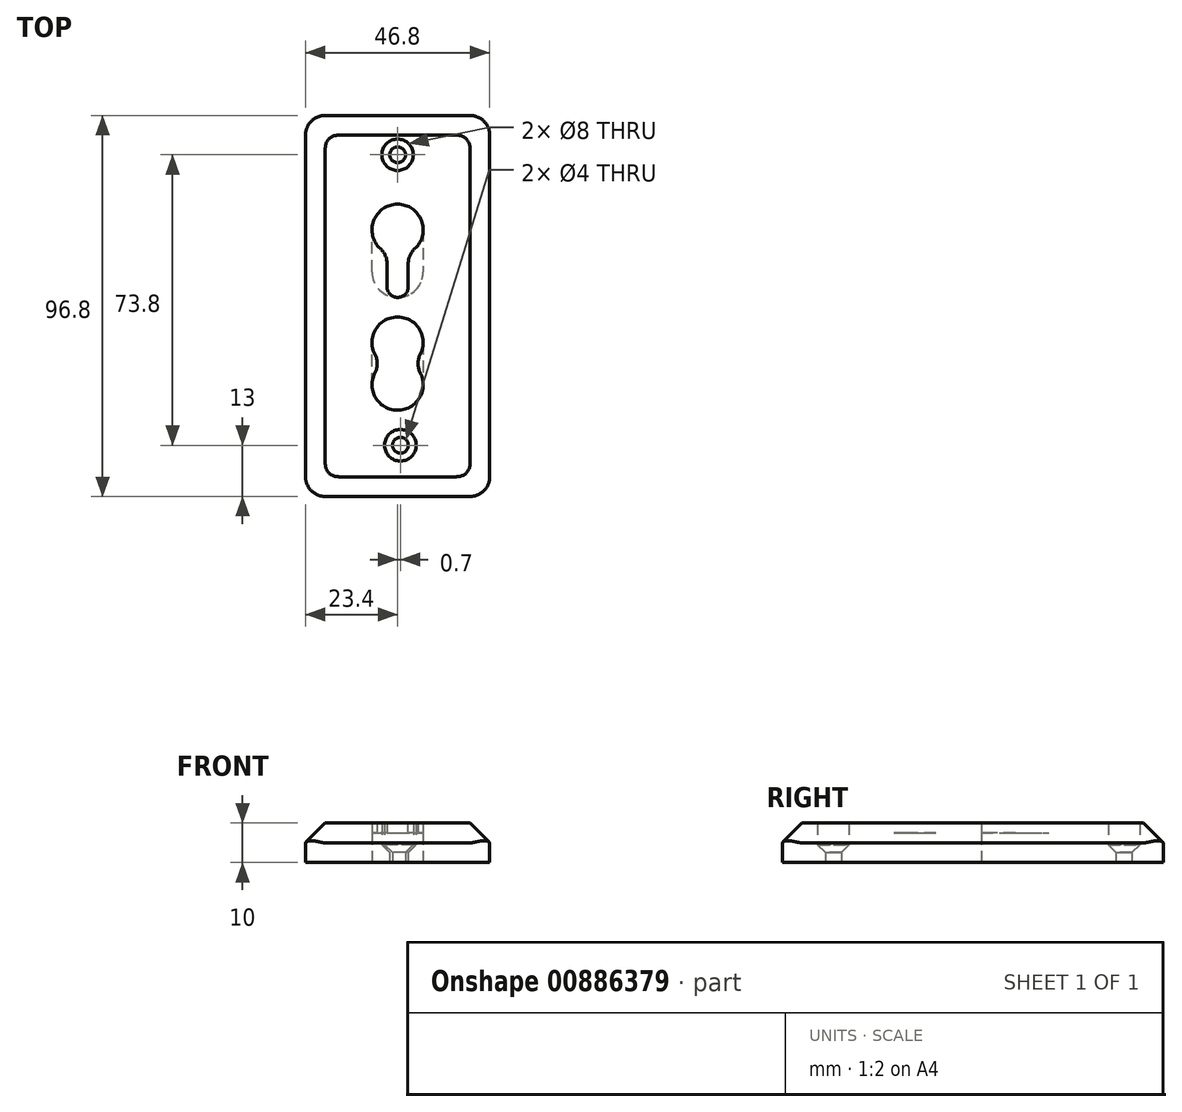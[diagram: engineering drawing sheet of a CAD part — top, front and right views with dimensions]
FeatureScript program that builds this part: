
annotation { "Feature Type Name" : "Feature", "Feature Type Description" : "" }
export const myFeature = defineFeature(function(context is Context, id is Id, definition is map)
    precondition{}
    {
        {
            var Q0;
            Q0=qCreatedBy(makeId("Top.planeOp"),FACE);
            var sketch = newSketch(context, id + "F0", { "sketchPlane" : qUnion([Q0])});
            skLineSegment(sketch, "E0", {"start": v(19.1, -41.4) * mm, "end": v(-17.7, -41.4) * mm});
            skCircle(sketch, "E1", {"center": v(0, -7.3) * mm, "radius": 6.5 * mm});
            skLineSegment(sketch, "E2", {"start": v(0, -7.3) * mm, "end": v(2.7, -7.3) * mm});
            skLineSegment(sketch, "E3.bottom", {"start": v(2.7, -7.3) * mm, "end": v(-2.7, -7.3) * mm});
            skLineSegment(sketch, "E4.top", {"start": v(-23.4, -46.4) * mm, "end": v(23.4, -46.4) * mm});
            skLineSegment(sketch, "E5", {"start": v(2.7, -7.3) * mm, "end": v(2.7, -21.8) * mm});
            skLineSegment(sketch, "E6", {"start": v(-2.7, -21.8) * mm, "end": v(-2.7, -7.3) * mm});
            skArc(sketch, "E7", {"start": v(2.7, -21.8) * mm, "mid": v(0, -24.5) * mm, "end": v(-2.7, -21.8) * mm});
            skLineSegment(sketch, "E8", {"start": v(0.7, -41.4) * mm, "end": v(0.7, -33.4) * mm});
            skCircle(sketch, "E9", {"center": v(0.7, -33.4) * mm, "radius": 2 * mm});
            skCircle(sketch, "E10", {"center": v(0.7, -33.4) * mm, "radius": 4 * mm});
            skLineSegment(sketch, "E11", {"start": v(19.1, 45.4) * mm, "end": v(-17.7, 45.4) * mm});
            skLineSegment(sketch, "E12", {"start": v(-17.7, 45.4) * mm, "end": v(-17.7, -41.4) * mm});
            skLineSegment(sketch, "E13", {"start": v(19.1, 45.4) * mm, "end": v(19.1, -41.4) * mm});
            skLineSegment(sketch, "E14", {"start": v(23.4, 50.4) * mm, "end": v(-23.4, 50.4) * mm});
            skLineSegment(sketch, "E15", {"start": v(-23.4, 50.4) * mm, "end": v(-23.4, -46.4) * mm});
            skLineSegment(sketch, "E16", {"start": v(23.4, 50.4) * mm, "end": v(23.4, -46.4) * mm});
            skLineSegment(sketch, "E17", {"start": v(0, 45.4) * mm, "end": v(0, 40.4) * mm});
            skCircle(sketch, "E18", {"center": v(0, 40.4) * mm, "radius": 2 * mm});
            skCircle(sketch, "E19", {"center": v(0, 40.4) * mm, "radius": 4 * mm});
            skCircle(sketch, "E20", {"center": v(0, -18) * mm, "radius": 6.5 * mm});
            skCircle(sketch, "E21", {"center": v(0, 21.35) * mm, "radius": 6.5 * mm});
            skLineSegment(sketch, "E22", {"start": v(0, 21.35) * mm, "end": v(2.7, 21.35) * mm});
            skLineSegment(sketch, "E23", {"start": v(2.7, 21.35) * mm, "end": v(2.7, 6.85) * mm});
            skLineSegment(sketch, "E24", {"start": v(-2.7, 6.85) * mm, "end": v(-2.7, 21.35) * mm});
            skLineSegment(sketch, "E25", {"start": v(-2.7, 21.35) * mm, "end": v(2.7, 21.35) * mm});
            skArc(sketch, "E26", {"start": v(2.7, 6.85) * mm, "mid": v(0, 4.15) * mm, "end": v(-2.7, 6.85) * mm});
            skCircle(sketch, "E27", {"center": v(0, 10.65) * mm, "radius": 6.5 * mm});
            skLineSegment(sketch, "E28", {"start": v(-6.5, 10.65) * mm, "end": v(-6.5, 21.35) * mm});
            skLineSegment(sketch, "E29", {"start": v(6.5, 21.35) * mm, "end": v(6.5, 10.65) * mm});
            skLineSegment(sketch, "E30", {"start": v(-6.5, -18) * mm, "end": v(-6.5, -7.3) * mm});
            skLineSegment(sketch, "E31", {"start": v(6.5, -7.3) * mm, "end": v(6.5, -18) * mm});
            skSolve(sketch);
        }
        {
            var Q0;
            Q0=makeQuery(id+"F0.imprint","IMPRINT",FACE,{"disambiguationData":[TD([[makeQuery(id+"F0.imprint","IMPRINT",EDGE,{"derivedFrom":sQuery(id+"F0.wireOp",EDGE,"E4.top")}),1.0]])]});
            var Q1;
            Q1=makeQuery(id+"F0.imprint","IMPRINT",FACE,{"disambiguationData":[TD([[makeQuery(id+"F0.imprint","IMPRINT",EDGE,{"derivedFrom":sQuery(id+"F0.wireOp",EDGE,"E10")}),-1.0]])]});
            var Q2;
            {var subQ0=sQuery(id+"F0.wireOp",EDGE,"E28");Q2=makeQuery(id+"F0.imprint","IMPRINT",FACE,{"disambiguationData":[TD([[makeQuery(id+"F0.imprint","IMPRINT",EDGE,{"derivedFrom":subQ0}),-1.0]])]});}
            var Q3;
            {var subQ0=sQuery(id+"F0.wireOp",EDGE,"E27");var subQ2=sQuery(id+"F0.wireOp",EDGE,"E21");var subQ3=makeQuery(id+"F0.imprint","INTERSECT",VERTEX,{"disambiguationData":[OD(0.0)],"derivedFrom":[subQ2,subQ0]});Q3=makeQuery(id+"F0.imprint","IMPRINT",FACE,{"disambiguationData":[TD([[makeQuery(id+"F0.imprint","IMPRINT",EDGE,{"disambiguationData":[TD([[subQ3,-1.0]])],"derivedFrom":subQ2}),-1.0]])]});}
            var Q4;
            {var subQ2=sQuery(id+"F0.wireOp",EDGE,"E21");var subQ5=sQuery(id+"F0.wireOp",EDGE,"E23");var subQ7=makeQuery(id+"F0.imprint","INTERSECT",VERTEX,{"derivedFrom":[subQ2,subQ5]});Q4=makeQuery(id+"F0.imprint","IMPRINT",FACE,{"disambiguationData":[TD([[makeQuery(id+"F0.imprint","IMPRINT",EDGE,{"disambiguationData":[TD([[subQ7,-1.0]])],"derivedFrom":subQ2}),-1.0]])]});}
            var Q5;
            {var subQ0=sQuery(id+"F0.wireOp",EDGE,"E29");Q5=makeQuery(id+"F0.imprint","IMPRINT",FACE,{"disambiguationData":[TD([[makeQuery(id+"F0.imprint","IMPRINT",EDGE,{"derivedFrom":subQ0}),-1.0]])]});}
            var Q6;
            {var subQ0=sQuery(id+"F0.wireOp",EDGE,"E30");Q6=makeQuery(id+"F0.imprint","IMPRINT",FACE,{"disambiguationData":[TD([[makeQuery(id+"F0.imprint","IMPRINT",EDGE,{"derivedFrom":subQ0}),-1.0]])]});}
            var Q7;
            {var subQ0=sQuery(id+"F0.wireOp",EDGE,"E20");var subQ9=makeQuery(id+"F0.imprint","IMPRINT",VERTEX,{"disambiguationData":[OD(1.0)],"derivedFrom":subQ0});Q7=makeQuery(id+"F0.imprint","IMPRINT",FACE,{"disambiguationData":[TD([[makeQuery(id+"F0.imprint","IMPRINT",EDGE,{"disambiguationData":[TD([[subQ9,1.0]])],"derivedFrom":subQ0}),1.0]])]});}
            var Q8;
            {var subQ0=sQuery(id+"F0.wireOp",EDGE,"E20");var subQ2=makeQuery(id+"F0.imprint","IMPRINT",VERTEX,{"disambiguationData":[OD(0.0)],"derivedFrom":subQ0});Q8=makeQuery(id+"F0.imprint","IMPRINT",FACE,{"disambiguationData":[TD([[makeQuery(id+"F0.imprint","IMPRINT",EDGE,{"disambiguationData":[TD([[subQ2,-1.0]])],"derivedFrom":subQ0}),1.0]])]});}
            var Q9;
            {var subQ0=sQuery(id+"F0.wireOp",EDGE,"E31");Q9=makeQuery(id+"F0.imprint","IMPRINT",FACE,{"disambiguationData":[TD([[makeQuery(id+"F0.imprint","IMPRINT",EDGE,{"derivedFrom":subQ0}),-1.0]])]});}
            extrude(context, id + "F1", {"entities" : qUnion([Q0, Q1, Q2, Q3, Q4, Q5, Q6, Q7, Q8, Q9]), "depth" : 10 * mm, "offsetDistance" : 25 * mm});
        }
        {
            var Q0;
            Q0=makeQuery(id+"F0.imprint","IMPRINT",FACE,{"disambiguationData":[TD([[makeQuery(id+"F0.imprint","IMPRINT",EDGE,{"derivedFrom":sQuery(id+"F0.wireOp",EDGE,"E9")}),-1.0]])]});
            var Q1;
            Q1=makeQuery(id+"F0.imprint","IMPRINT",FACE,{"disambiguationData":[TD([[makeQuery(id+"F0.imprint","IMPRINT",EDGE,{"derivedFrom":sQuery(id+"F0.wireOp",EDGE,"E18")}),-1.0]])]});
            extrude(context, id + "F2", {"entities" : qUnion([Q0, Q1]), "operationType" : NewBodyOperationType.ADD, "depth" : 5 * mm, "offsetDistance" : 25 * mm});
        }
        {
            var Q0;
            {var subQ0=sQuery(id+"F0.wireOp",EDGE,"E29");Q0=makeQuery(id+"F0.imprint","IMPRINT",FACE,{"disambiguationData":[TD([[makeQuery(id+"F0.imprint","IMPRINT",EDGE,{"derivedFrom":subQ0}),-1.0]])]});}
            var Q1;
            {var subQ2=sQuery(id+"F0.wireOp",EDGE,"E21");var subQ5=sQuery(id+"F0.wireOp",EDGE,"E23");var subQ7=makeQuery(id+"F0.imprint","INTERSECT",VERTEX,{"derivedFrom":[subQ2,subQ5]});Q1=makeQuery(id+"F0.imprint","IMPRINT",FACE,{"disambiguationData":[TD([[makeQuery(id+"F0.imprint","IMPRINT",EDGE,{"disambiguationData":[TD([[subQ7,-1.0]])],"derivedFrom":subQ2}),-1.0]])]});}
            var Q2;
            {var subQ0=sQuery(id+"F0.wireOp",EDGE,"E27");var subQ2=sQuery(id+"F0.wireOp",EDGE,"E21");var subQ3=makeQuery(id+"F0.imprint","INTERSECT",VERTEX,{"disambiguationData":[OD(0.0)],"derivedFrom":[subQ2,subQ0]});Q2=makeQuery(id+"F0.imprint","IMPRINT",FACE,{"disambiguationData":[TD([[makeQuery(id+"F0.imprint","IMPRINT",EDGE,{"disambiguationData":[TD([[subQ3,-1.0]])],"derivedFrom":subQ2}),-1.0]])]});}
            var Q3;
            {var subQ0=sQuery(id+"F0.wireOp",EDGE,"E28");Q3=makeQuery(id+"F0.imprint","IMPRINT",FACE,{"disambiguationData":[TD([[makeQuery(id+"F0.imprint","IMPRINT",EDGE,{"derivedFrom":subQ0}),-1.0]])]});}
            var Q4;
            {var subQ0=sQuery(id+"F0.wireOp",EDGE,"E30");Q4=makeQuery(id+"F0.imprint","IMPRINT",FACE,{"disambiguationData":[TD([[makeQuery(id+"F0.imprint","IMPRINT",EDGE,{"derivedFrom":subQ0}),-1.0]])]});}
            var Q5;
            {var subQ0=sQuery(id+"F0.wireOp",EDGE,"E20");var subQ9=makeQuery(id+"F0.imprint","IMPRINT",VERTEX,{"disambiguationData":[OD(1.0)],"derivedFrom":subQ0});Q5=makeQuery(id+"F0.imprint","IMPRINT",FACE,{"disambiguationData":[TD([[makeQuery(id+"F0.imprint","IMPRINT",EDGE,{"disambiguationData":[TD([[subQ9,1.0]])],"derivedFrom":subQ0}),1.0]])]});}
            var Q6;
            {var subQ0=sQuery(id+"F0.wireOp",EDGE,"E20");var subQ2=makeQuery(id+"F0.imprint","IMPRINT",VERTEX,{"disambiguationData":[OD(0.0)],"derivedFrom":subQ0});Q6=makeQuery(id+"F0.imprint","IMPRINT",FACE,{"disambiguationData":[TD([[makeQuery(id+"F0.imprint","IMPRINT",EDGE,{"disambiguationData":[TD([[subQ2,-1.0]])],"derivedFrom":subQ0}),1.0]])]});}
            var Q7;
            {var subQ0=sQuery(id+"F0.wireOp",EDGE,"E31");Q7=makeQuery(id+"F0.imprint","IMPRINT",FACE,{"disambiguationData":[TD([[makeQuery(id+"F0.imprint","IMPRINT",EDGE,{"derivedFrom":subQ0}),-1.0]])]});}
            extrude(context, id + "F3", {"entities" : qUnion([Q0, Q1, Q2, Q3, Q4, Q5, Q6, Q7]), "operationType" : NewBodyOperationType.REMOVE, "depth" : 7.5 * mm, "offsetDistance" : 25 * mm});
        }
        {
            var Q0;
            Q0=makeQuery(id+"F2.opExtrude","CAP_EDGE",EDGE,{"disambiguationData":[OSD([sQuery(id+"F0.wireOp",EDGE,"E18")])],"isStart":false});
            chamfer(context, id + "F4", {"entities" : qUnion([Q0]), "width" : 2.5 * mm, "tangentPropagation" : true});
        }
        {
            var Q0;
            Q0=makeQuery(id+"F2.opExtrude","CAP_EDGE",EDGE,{"disambiguationData":[OSD([sQuery(id+"F0.wireOp",EDGE,"E9")])],"isStart":false});
            chamfer(context, id + "F5", {"entities" : qUnion([Q0]), "width" : 2.5 * mm, "tangentPropagation" : true});
        }
        {
            var Q0;
            Q0=makeQuery(id+"F1.opExtrude","CAP_EDGE",EDGE,{"disambiguationData":[OSD([sQuery(id+"F0.wireOp",EDGE,"E4.top")])],"isStart":false});
            var Q1;
            Q1=makeQuery(id+"F1.opExtrude","CAP_EDGE",EDGE,{"disambiguationData":[OSD([sQuery(id+"F0.wireOp",EDGE,"E14")])],"isStart":false});
            chamfer(context, id + "F6", {"entities" : qUnion([Q0, Q1]), "width" : 5 * mm, "tangentPropagation" : true});
        }
        {
            var Q0;
            Q0=makeQuery(id+"F1.opExtrude","CAP_EDGE",EDGE,{"disambiguationData":[OSD([sQuery(id+"F0.wireOp",EDGE,"E16")])],"isStart":false});
            var Q1;
            Q1=makeQuery(id+"F1.opExtrude","CAP_EDGE",EDGE,{"disambiguationData":[OSD([sQuery(id+"F0.wireOp",EDGE,"E15")])],"isStart":false});
            chamfer(context, id + "F7", {"entities" : qUnion([Q0, Q1]), "width" : 5 * mm, "tangentPropagation" : true});
        }
        {
            var Q0;
            Q0=makeQuery(id+"F1.opExtrude","SWEPT_EDGE",EDGE,{"disambiguationData":[OSD([sQuery(id+"F0.wireOp",EDGE,"E1"),sQuery(id+"F0.wireOp",EDGE,"E6")])]});
            var Q1;
            Q1=makeQuery(id+"F1.opExtrude","SWEPT_EDGE",EDGE,{"disambiguationData":[OSD([sQuery(id+"F0.wireOp",EDGE,"E1"),sQuery(id+"F0.wireOp",EDGE,"E5")])]});
            var Q2;
            Q2=makeQuery(id+"F1.opExtrude","SWEPT_EDGE",EDGE,{"disambiguationData":[OSD([sQuery(id+"F0.wireOp",EDGE,"E21"),sQuery(id+"F0.wireOp",EDGE,"E23")])]});
            var Q3;
            Q3=makeQuery(id+"F1.opExtrude","SWEPT_EDGE",EDGE,{"disambiguationData":[OSD([sQuery(id+"F0.wireOp",EDGE,"E21"),sQuery(id+"F0.wireOp",EDGE,"E24")])]});
            fillet(context, id + "F8", {"entities" : qUnion([Q0, Q1, Q2, Q3]), "radius" : 5 * mm, "tangentPropagation" : true, "allowEdgeOverflow" : false});
        }
        {
            var Q0;
            Q0=makeQuery(id+"F7.opChamfer","BLEND_EDGE",EDGE,{"blendedFrom":[makeQuery(id+"F1.opExtrude","CAP_EDGE",EDGE,{"disambiguationData":[OSD([sQuery(id+"F0.wireOp",EDGE,"E16")])],"isStart":false}),makeQuery(id+"F6.opChamfer","BLEND_FACE",FACE,{"disambiguationData":[OSD([sQuery(id+"F0.wireOp",EDGE,"E4.top")])]})],"blendedInto":[makeQuery(id+"F6.opChamfer","BLEND_FACE",FACE,{"disambiguationData":[OSD([sQuery(id+"F0.wireOp",EDGE,"E4.top")])]})]});
            var Q1;
            Q1=makeQuery(id+"F7.opChamfer","BLEND_EDGE",EDGE,{"blendedFrom":[makeQuery(id+"F1.opExtrude","CAP_EDGE",EDGE,{"disambiguationData":[OSD([sQuery(id+"F0.wireOp",EDGE,"E15")])],"isStart":false}),makeQuery(id+"F6.opChamfer","BLEND_FACE",FACE,{"disambiguationData":[OSD([sQuery(id+"F0.wireOp",EDGE,"E4.top")])]})],"blendedInto":[makeQuery(id+"F6.opChamfer","BLEND_FACE",FACE,{"disambiguationData":[OSD([sQuery(id+"F0.wireOp",EDGE,"E4.top")])]})]});
            var Q2;
            Q2=makeQuery(id+"F7.opChamfer","BLEND_EDGE",EDGE,{"blendedFrom":[makeQuery(id+"F1.opExtrude","CAP_EDGE",EDGE,{"disambiguationData":[OSD([sQuery(id+"F0.wireOp",EDGE,"E16")])],"isStart":false}),makeQuery(id+"F6.opChamfer","BLEND_FACE",FACE,{"disambiguationData":[OSD([sQuery(id+"F0.wireOp",EDGE,"E14")])]})],"blendedInto":[makeQuery(id+"F6.opChamfer","BLEND_FACE",FACE,{"disambiguationData":[OSD([sQuery(id+"F0.wireOp",EDGE,"E14")])]})]});
            var Q3;
            Q3=makeQuery(id+"F7.opChamfer","BLEND_EDGE",EDGE,{"blendedFrom":[makeQuery(id+"F1.opExtrude","CAP_EDGE",EDGE,{"disambiguationData":[OSD([sQuery(id+"F0.wireOp",EDGE,"E15")])],"isStart":false}),makeQuery(id+"F6.opChamfer","BLEND_FACE",FACE,{"disambiguationData":[OSD([sQuery(id+"F0.wireOp",EDGE,"E14")])]})],"blendedInto":[makeQuery(id+"F6.opChamfer","BLEND_FACE",FACE,{"disambiguationData":[OSD([sQuery(id+"F0.wireOp",EDGE,"E14")])]})]});
            fillet(context, id + "F9", {"entities" : qUnion([Q0, Q1, Q2, Q3]), "radius" : 5 * mm, "tangentPropagation" : true, "allowEdgeOverflow" : false});
        }
        {
            var Q0;
            Q0=makeQuery(id+"F1.opExtrude","SWEPT_EDGE",EDGE,{"disambiguationData":[OSD([sQuery(id+"F0.wireOp",EDGE,"E14"),sQuery(id+"F0.wireOp",EDGE,"E15")])]});
            var Q1;
            Q1=makeQuery(id+"F1.opExtrude","SWEPT_EDGE",EDGE,{"disambiguationData":[OSD([sQuery(id+"F0.wireOp",EDGE,"E14"),sQuery(id+"F0.wireOp",EDGE,"E16")])]});
            var Q2;
            Q2=makeQuery(id+"F1.opExtrude","SWEPT_EDGE",EDGE,{"disambiguationData":[OSD([sQuery(id+"F0.wireOp",EDGE,"E4.top"),sQuery(id+"F0.wireOp",EDGE,"E16")])]});
            var Q3;
            Q3=makeQuery(id+"F1.opExtrude","SWEPT_EDGE",EDGE,{"disambiguationData":[OSD([sQuery(id+"F0.wireOp",EDGE,"E4.top"),sQuery(id+"F0.wireOp",EDGE,"E15")])]});
            fillet(context, id + "F10", {"entities" : qUnion([Q0, Q1, Q2, Q3]), "radius" : 5 * mm, "tangentPropagation" : true, "allowEdgeOverflow" : false});
        }
    });
